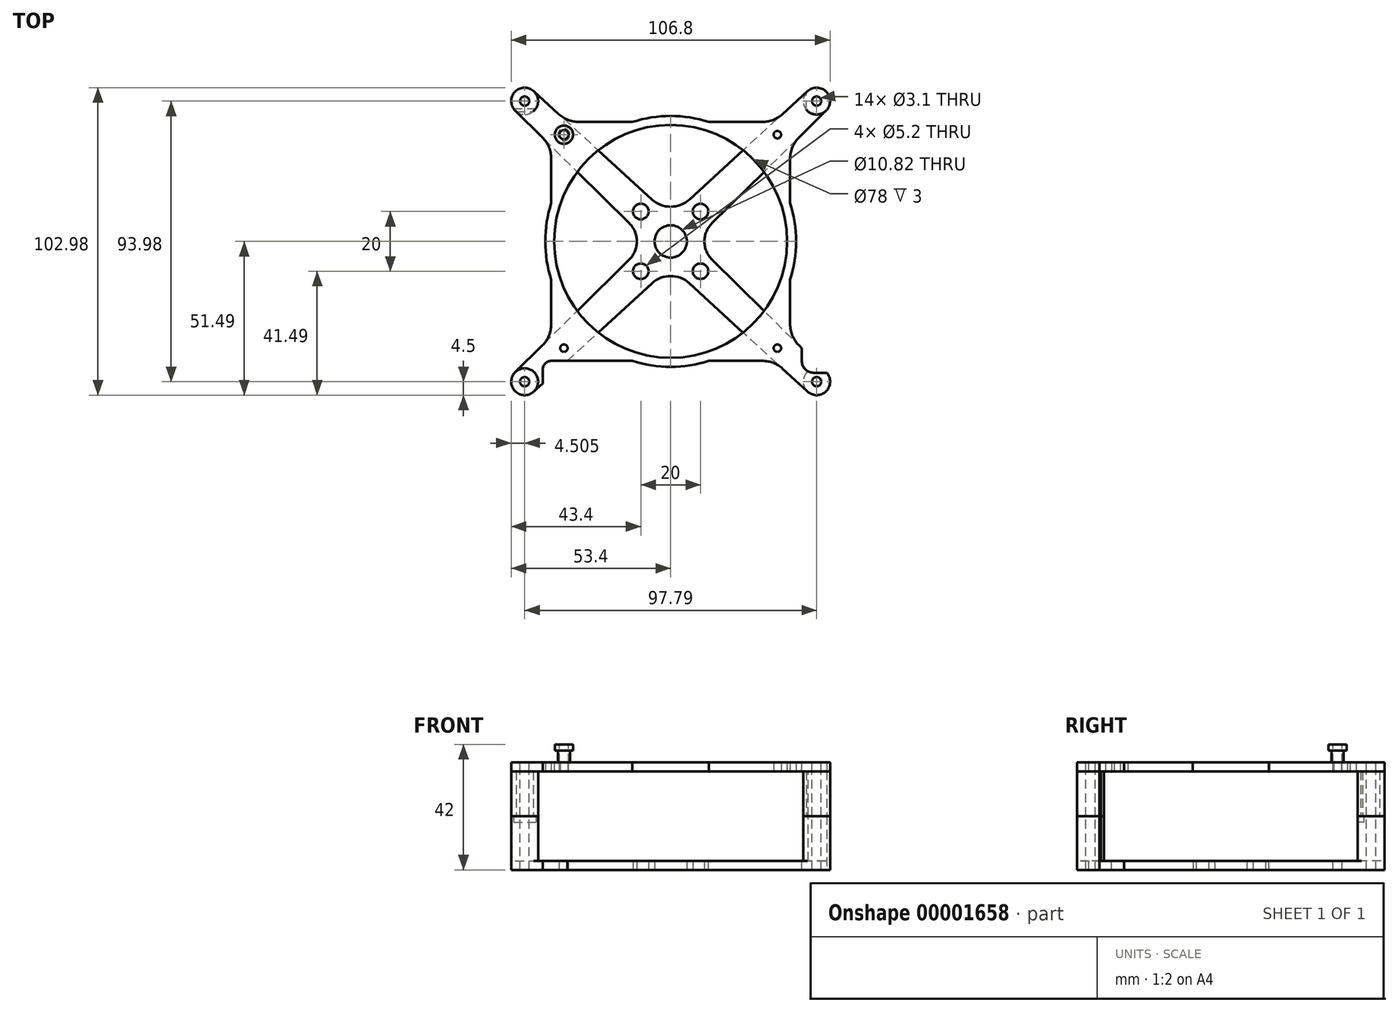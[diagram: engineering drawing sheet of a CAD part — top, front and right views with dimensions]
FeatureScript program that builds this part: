
annotation { "Feature Type Name" : "Feature", "Feature Type Description" : "" }
export const myFeature = defineFeature(function(context is Context, id is Id, definition is map)
    precondition{}
    {
        {
            var Q0;
            Q0=qCreatedBy(makeId("Top.planeOp"),FACE);
            var sketch = newSketch(context, id + "F0", { "sketchPlane" : qUnion([Q0])});
            skLineSegment(sketch, "E0.rect.bottom", {"start": v(48.9, 46.99) * mm, "end": v(-48.9, 46.99) * mm, "construction": true});
            skLineSegment(sketch, "E0.rect.top", {"start": v(48.9, -47) * mm, "end": v(-48.9, -47) * mm, "construction": true});
            skLineSegment(sketch, "E0.rect.left", {"start": v(48.9, 46.99) * mm, "end": v(48.9, -47) * mm, "construction": true});
            skLineSegment(sketch, "E0.rect.right", {"start": v(-48.9, 46.99) * mm, "end": v(-48.9, -47) * mm, "construction": true});
            skPoint(sketch, "E0.rect.middle", {"position": v(0, 0) * mm});
            skLineSegment(sketch, "E1.rect.bottom", {"start": v(10, 10) * mm, "end": v(-10, 10) * mm, "construction": true});
            skLineSegment(sketch, "E1.rect.top", {"start": v(10, -10) * mm, "end": v(-10, -10) * mm, "construction": true});
            skLineSegment(sketch, "E1.rect.left", {"start": v(10, 10) * mm, "end": v(10, -10) * mm, "construction": true});
            skLineSegment(sketch, "E1.rect.right", {"start": v(-10, 10) * mm, "end": v(-10, -10) * mm, "construction": true});
            skCircle(sketch, "E2", {"center": v(-10, 10) * mm, "radius": 2.6 * mm});
            skCircle(sketch, "E3", {"center": v(10, 10) * mm, "radius": 2.6 * mm});
            skCircle(sketch, "E4", {"center": v(10, -10) * mm, "radius": 2.6 * mm});
            skCircle(sketch, "E5", {"center": v(-10, -10) * mm, "radius": 2.6 * mm});
            skArc(sketch, "E6", {"start": v(-45.86, 50.3) * mm, "mid": v(-52.16, 50.1) * mm, "end": v(-52.06, 43.79) * mm});
            skArc(sketch, "E7", {"start": v(52.06, 43.79) * mm, "mid": v(52.16, 50.1) * mm, "end": v(45.86, 50.3) * mm});
            skArc(sketch, "E8", {"start": v(45.86, -50.3) * mm, "mid": v(52.16, -50.1) * mm, "end": v(52.06, -43.79) * mm});
            skArc(sketch, "E9", {"start": v(-52.06, -43.79) * mm, "mid": v(-52.16, -50.1) * mm, "end": v(-45.86, -50.3) * mm});
            skCircle(sketch, "E10", {"center": v(-10, -10) * mm, "radius": 5.5 * mm, "construction": true});
            skCircle(sketch, "E11", {"center": v(10, -10) * mm, "radius": 5.5 * mm, "construction": true});
            skCircle(sketch, "E12", {"center": v(-10, 10) * mm, "radius": 5.5 * mm, "construction": true});
            skCircle(sketch, "E13", {"center": v(10, 10) * mm, "radius": 5.5 * mm, "construction": true});
            skArc(sketch, "E14", {"start": v(-13.86, -6.09) * mm, "mid": v(-11.32, 0) * mm, "end": v(-13.86, 6.09) * mm});
            skLineSegment(sketch, "E15", {"start": v(-52.06, -43.79) * mm, "end": v(-13.86, -6.09) * mm});
            skLineSegment(sketch, "E16", {"start": v(-45.86, -50.3) * mm, "end": v(-6.28, -14.06) * mm});
            skLineSegment(sketch, "E17", {"start": v(45.86, 50.3) * mm, "end": v(6.28, 14.06) * mm});
            skLineSegment(sketch, "E18", {"start": v(52.06, 43.79) * mm, "end": v(13.86, 6.09) * mm});
            skLineSegment(sketch, "E19", {"start": v(-52.06, 43.79) * mm, "end": v(-13.86, 6.09) * mm});
            skLineSegment(sketch, "E20", {"start": v(-45.86, 50.3) * mm, "end": v(-6.28, 14.06) * mm});
            skLineSegment(sketch, "E21", {"start": v(45.86, -50.3) * mm, "end": v(6.28, -14.06) * mm});
            skLineSegment(sketch, "E22", {"start": v(52.06, -43.79) * mm, "end": v(13.86, -6.09) * mm});
            skArc(sketch, "E23", {"start": v(-6.28, 14.06) * mm, "mid": v(0, 11.61) * mm, "end": v(6.28, 14.06) * mm});
            skArc(sketch, "E24", {"start": v(13.86, 6.09) * mm, "mid": v(11.32, 0) * mm, "end": v(13.86, -6.09) * mm});
            skArc(sketch, "E25", {"start": v(6.28, -14.06) * mm, "mid": v(0, -11.61) * mm, "end": v(-6.28, -14.06) * mm});
            skCircle(sketch, "E26", {"center": v(0, 0) * mm, "radius": 5.4 * mm});
            skSolve(sketch);
        }
        {
            var Q0;
            Q0 = qSketchRegion(id + "F0", true);
            extrude(context, id + "F1", {"entities" : qUnion([Q0]), "depth" : 3 * mm});
        }
        {
            var Q0;
            Q0=makeQuery(id+"F1.opExtrude","CAP_FACE",FACE,{"disambiguationData":[OSD([sQuery(id+"F0.wireOp",EDGE,"d0fabe0d-cebb-4a5e-acc7-4882b4730778"),sQuery(id+"F0.wireOp",EDGE,"8b31ac3e-8670-4111-bd45-4e3589581e22"),sQuery(id+"F0.wireOp",EDGE,"b8c4f240-0c61-4009-8258-f043c920e522"),sQuery(id+"F0.wireOp",EDGE,"c1348664-0ed1-4957-8f92-31a3f3ab937f"),sQuery(id+"F0.wireOp",EDGE,"E2"),sQuery(id+"F0.wireOp",EDGE,"E3"),sQuery(id+"F0.wireOp",EDGE,"E4"),sQuery(id+"F0.wireOp",EDGE,"E5"),sQuery(id+"F0.wireOp",EDGE,"E6"),sQuery(id+"F0.wireOp",EDGE,"E7"),sQuery(id+"F0.wireOp",EDGE,"E8"),sQuery(id+"F0.wireOp",EDGE,"E9"),sQuery(id+"F0.wireOp",EDGE,"E14"),sQuery(id+"F0.wireOp",EDGE,"E15"),sQuery(id+"F0.wireOp",EDGE,"E16"),sQuery(id+"F0.wireOp",EDGE,"E17"),sQuery(id+"F0.wireOp",EDGE,"E18"),sQuery(id+"F0.wireOp",EDGE,"E19"),sQuery(id+"F0.wireOp",EDGE,"E20"),sQuery(id+"F0.wireOp",EDGE,"E21"),sQuery(id+"F0.wireOp",EDGE,"E22"),sQuery(id+"F0.wireOp",EDGE,"E23"),sQuery(id+"F0.wireOp",EDGE,"E24"),sQuery(id+"F0.wireOp",EDGE,"E25"),sQuery(id+"F0.wireOp",EDGE,"E26")])],"isStart":false});
            var sketch = newSketch(context, id + "F2", { "sketchPlane" : qUnion([Q0])});
            skCircle(sketch, "E27", {"center": v(-48.9, 46.99) * mm, "radius": 4.5 * mm});
            skCircle(sketch, "E28", {"center": v(48.9, 46.99) * mm, "radius": 4.5 * mm});
            skCircle(sketch, "E29", {"center": v(48.9, -47) * mm, "radius": 4.5 * mm});
            skCircle(sketch, "E30", {"center": v(-48.9, -47) * mm, "radius": 4.5 * mm});
            skSolve(sketch);
        }
        {
            var Q0;
            Q0 = qSketchRegion(id + "F2", true);
            extrude(context, id + "F3", {"entities" : qUnion([Q0]), "operationType" : NewBodyOperationType.ADD, "depth" : 15 * mm});
        }
        {
            var Q0;
            Q0=makeQuery(id+"F3.opExtrude","CAP_FACE",FACE,{"disambiguationData":[OSD([sQuery(id+"F2.wireOp",EDGE,"E27")])],"isStart":false});
            var sketch = newSketch(context, id + "F4", { "sketchPlane" : qUnion([Q0])});
            skCircle(sketch, "E31", {"center": v(-48.9, 46.99) * mm, "radius": 1.25 * mm});
            skCircle(sketch, "E32", {"center": v(48.9, 46.99) * mm, "radius": 1.25 * mm});
            skCircle(sketch, "E33", {"center": v(-48.9, -47) * mm, "radius": 1.25 * mm});
            skCircle(sketch, "E34", {"center": v(48.9, -47) * mm, "radius": 1.25 * mm});
            skSolve(sketch);
        }
        {
            var Q0;
            Q0 = qSketchRegion(id + "F4", true);
            extrude(context, id + "F5", {"entities" : qUnion([Q0]), "operationType" : NewBodyOperationType.REMOVE, "endBound" : BoundingType.THROUGH_ALL, "oppositeDirection" : true, "depth" : 25 * mm});
        }
        {
            var Q0;
            Q0=makeQuery(id+"F3.opExtrude","CAP_FACE",FACE,{"disambiguationData":[OSD([sQuery(id+"F2.wireOp",EDGE,"E27")])],"isStart":false});
            var sketch = newSketch(context, id + "F6", { "sketchPlane" : qUnion([Q0])});
            skArc(sketch, "E35", {"start": v(-46.07, 43.49) * mm, "mid": v(-48.9, 51.49) * mm, "end": v(-51.72, 43.49) * mm});
            skArc(sketch, "E36", {"start": v(45.4, 44.16) * mm, "mid": v(53.4, 47) * mm, "end": v(45.4, 49.82) * mm});
            skArc(sketch, "E37", {"start": v(46.07, -43.5) * mm, "mid": v(48.9, -51.5) * mm, "end": v(51.72, -43.5) * mm});
            skCircle(sketch, "E38", {"center": v(-48.9, -47) * mm, "radius": 4.5 * mm});
            skLineSegment(sketch, "E39", {"start": v(-51.72, 43.49) * mm, "end": v(-46.07, 43.49) * mm});
            skLineSegment(sketch, "E40", {"start": v(45.4, 44.16) * mm, "end": v(45.4, 49.82) * mm});
            skLineSegment(sketch, "E41", {"start": v(46.07, -43.5) * mm, "end": v(51.72, -43.5) * mm});
            skSolve(sketch);
        }
        {
            var Q0;
            Q0 = qSketchRegion(id + "F6", true);
            extrude(context, id + "F7", {"entities" : qUnion([Q0]), "depth" : 15 * mm});
        }
        {
            var Q0;
            Q0=makeQuery(id+"F7.opExtrude","CAP_FACE",FACE,{"disambiguationData":[OSD([sQuery(id+"F6.wireOp",EDGE,"E35")])],"isStart":false});
            var sketch = newSketch(context, id + "F8", { "sketchPlane" : qUnion([Q0])});
            skLineSegment(sketch, "E42.rect.bottom", {"start": v(35.75, 35.75) * mm, "end": v(-35.75, 35.75) * mm, "construction": true});
            skLineSegment(sketch, "E42.rect.top", {"start": v(35.75, -35.75) * mm, "end": v(-35.75, -35.75) * mm, "construction": true});
            skLineSegment(sketch, "E42.rect.left", {"start": v(35.75, 35.75) * mm, "end": v(35.75, -35.75) * mm, "construction": true});
            skLineSegment(sketch, "E42.rect.right", {"start": v(-35.75, 35.75) * mm, "end": v(-35.75, -35.75) * mm, "construction": true});
            skPoint(sketch, "E42.rect.middle", {"position": v(0, 0) * mm});
            skCircle(sketch, "E43", {"center": v(-35.75, 35.75) * mm, "radius": 1.25 * mm});
            skCircle(sketch, "E44", {"center": v(35.75, 35.75) * mm, "radius": 1.25 * mm});
            skCircle(sketch, "E45", {"center": v(35.75, -35.75) * mm, "radius": 1.25 * mm});
            skCircle(sketch, "E46", {"center": v(-35.75, -35.75) * mm, "radius": 1.25 * mm});
            skCircle(sketch, "E47", {"center": v(0, 0) * mm, "radius": 39 * mm});
            skArc(sketch, "E48", {"start": v(-52.06, -43.79) * mm, "mid": v(-52.16, -50.1) * mm, "end": v(-45.86, -50.3) * mm});
            skArc(sketch, "E49", {"start": v(45.86, -50.3) * mm, "mid": v(52.16, -50.1) * mm, "end": v(52.06, -43.79) * mm});
            skArc(sketch, "E50", {"start": v(52.06, 43.79) * mm, "mid": v(52.16, 50.1) * mm, "end": v(45.86, 50.3) * mm});
            skArc(sketch, "E51", {"start": v(-45.86, 50.3) * mm, "mid": v(-52.16, 50.1) * mm, "end": v(-52.06, 43.79) * mm});
            skLineSegment(sketch, "E52", {"start": v(-52.06, 43.79) * mm, "end": v(-42.97, 34.82) * mm});
            skLineSegment(sketch, "E53", {"start": v(-45.86, 50.3) * mm, "end": v(-37.47, 42.63) * mm});
            skLineSegment(sketch, "E54", {"start": v(45.86, 50.3) * mm, "end": v(37.47, 42.63) * mm});
            skLineSegment(sketch, "E55", {"start": v(52.06, 43.79) * mm, "end": v(42.97, 34.82) * mm});
            skLineSegment(sketch, "E56", {"start": v(52.06, -43.79) * mm, "end": v(42.97, -34.82) * mm});
            skLineSegment(sketch, "E57", {"start": v(45.86, -50.3) * mm, "end": v(37.47, -42.63) * mm});
            skLineSegment(sketch, "E58", {"start": v(-45.86, -50.3) * mm, "end": v(-37.47, -42.63) * mm});
            skLineSegment(sketch, "E59", {"start": v(-52.06, -43.79) * mm, "end": v(-42.97, -34.82) * mm});
            skLineSegment(sketch, "E60.rect.bottom", {"start": v(30.72, 40) * mm, "end": v(12.8, 40) * mm});
            skLineSegment(sketch, "E60.rect.top", {"start": v(30.72, -40) * mm, "end": v(12.8, -40) * mm});
            skLineSegment(sketch, "E60.rect.left", {"start": v(40, 27.7) * mm, "end": v(40, 12.8) * mm});
            skLineSegment(sketch, "E60.rect.right", {"start": v(-40, 27.7) * mm, "end": v(-40, 12.8) * mm});
            skPoint(sketch, "E61.orphan", {"position": v(-40, 40) * mm});
            skPoint(sketch, "E62.orphan", {"position": v(-40, -40) * mm});
            skLineSegment(sketch, "E63.trimOffspring", {"start": v(-40, -12.8) * mm, "end": v(-40, -27.7) * mm});
            skPoint(sketch, "E64.orphan", {"position": v(40, -40) * mm});
            skLineSegment(sketch, "E65.trimOffspring", {"start": v(40, -12.8) * mm, "end": v(40, -27.7) * mm});
            skPoint(sketch, "E66.orphan", {"position": v(40, 40) * mm});
            skArc(sketch, "E67.trimOffspring", {"start": v(12.8, 40) * mm, "mid": v(0, 42) * mm, "end": v(-12.8, 40) * mm});
            skLineSegment(sketch, "E68.trimOffspring", {"start": v(-12.8, 40) * mm, "end": v(-30.72, 40) * mm});
            skArc(sketch, "E69.trimOffspring", {"start": v(-40, 12.8) * mm, "mid": v(-42, 0) * mm, "end": v(-40, -12.8) * mm});
            skArc(sketch, "E70.trimOffspring", {"start": v(40, -12.8) * mm, "mid": v(42, 0) * mm, "end": v(40, 12.8) * mm});
            skLineSegment(sketch, "E71.trimOffspring", {"start": v(-12.8, -40) * mm, "end": v(-30.72, -40) * mm});
            skArc(sketch, "E72.trimOffspring", {"start": v(-12.8, -40) * mm, "mid": v(0, -42) * mm, "end": v(12.8, -40) * mm});
            skPoint(sketch, "E73.visualSharp", {"position": v(-40, 31.89) * mm});
            skArc(sketch, "E73.filletArc", {"start": v(-40, 27.7) * mm, "mid": v(-40.77, 31.56) * mm, "end": v(-42.97, 34.82) * mm});
            skPoint(sketch, "E74.visualSharp", {"position": v(-40, -31.89) * mm});
            skArc(sketch, "E74.filletArc", {"start": v(-42.97, -34.82) * mm, "mid": v(-40.77, -31.56) * mm, "end": v(-40, -27.7) * mm});
            skPoint(sketch, "E75.visualSharp", {"position": v(-34.6, -40) * mm});
            skArc(sketch, "E75.filletArc", {"start": v(-30.72, -40) * mm, "mid": v(-34.34, -40.68) * mm, "end": v(-37.47, -42.63) * mm});
            skPoint(sketch, "E76.visualSharp", {"position": v(34.6, -40) * mm});
            skArc(sketch, "E76.filletArc", {"start": v(37.47, -42.63) * mm, "mid": v(34.34, -40.68) * mm, "end": v(30.72, -40) * mm});
            skPoint(sketch, "E77.visualSharp", {"position": v(40, -31.89) * mm});
            skArc(sketch, "E77.filletArc", {"start": v(40, -27.7) * mm, "mid": v(40.77, -31.56) * mm, "end": v(42.97, -34.82) * mm});
            skPoint(sketch, "E78.visualSharp", {"position": v(40, 31.89) * mm});
            skArc(sketch, "E78.filletArc", {"start": v(42.97, 34.82) * mm, "mid": v(40.77, 31.56) * mm, "end": v(40, 27.7) * mm});
            skPoint(sketch, "E79.visualSharp", {"position": v(34.6, 40) * mm});
            skArc(sketch, "E79.filletArc", {"start": v(30.72, 40) * mm, "mid": v(34.34, 40.68) * mm, "end": v(37.47, 42.63) * mm});
            skPoint(sketch, "E80.visualSharp", {"position": v(-34.6, 40) * mm});
            skArc(sketch, "E80.filletArc", {"start": v(-37.47, 42.63) * mm, "mid": v(-34.34, 40.68) * mm, "end": v(-30.72, 40) * mm});
            skSolve(sketch);
        }
        {
            var Q0;
            Q0 = qSketchRegion(id + "F8", true);
            extrude(context, id + "F9", {"entities" : qUnion([Q0]), "depth" : 3 * mm});
        }
        {
            var Q0;
            Q0=makeQuery(id+"F9.opExtrude","CAP_FACE",FACE,{"disambiguationData":[OSD([sQuery(id+"F8.wireOp",EDGE,"E43"),sQuery(id+"F8.wireOp",EDGE,"E44"),sQuery(id+"F8.wireOp",EDGE,"E45"),sQuery(id+"F8.wireOp",EDGE,"E46"),sQuery(id+"F8.wireOp",EDGE,"E47"),sQuery(id+"F8.wireOp",EDGE,"687bd6d6-6aec-43aa-978a-a651606573d6"),sQuery(id+"F8.wireOp",EDGE,"E48"),sQuery(id+"F8.wireOp",EDGE,"E49"),sQuery(id+"F8.wireOp",EDGE,"E50"),sQuery(id+"F8.wireOp",EDGE,"E51"),sQuery(id+"F8.wireOp",EDGE,"E52"),sQuery(id+"F8.wireOp",EDGE,"E53"),sQuery(id+"F8.wireOp",EDGE,"E54"),sQuery(id+"F8.wireOp",EDGE,"E55"),sQuery(id+"F8.wireOp",EDGE,"E56"),sQuery(id+"F8.wireOp",EDGE,"E57"),sQuery(id+"F8.wireOp",EDGE,"E58"),sQuery(id+"F8.wireOp",EDGE,"E59"),sQuery(id+"F8.wireOp",EDGE,"161f5221-b585-4942-8812-eb4c8e719fd1.trimOffspring"),sQuery(id+"F8.wireOp",EDGE,"33abffde-fc44-4a8e-acad-815204f06dd8.trimOffspring"),sQuery(id+"F8.wireOp",EDGE,"e672300c-3f6b-4d4b-81d5-837dd4541bc1.trimOffspring")])],"isStart":false});
            var sketch = newSketch(context, id + "F10", { "sketchPlane" : qUnion([Q0])});
            skCircle(sketch, "E81", {"center": v(-48.9, 46.99) * mm, "radius": 1.55 * mm});
            skCircle(sketch, "E82", {"center": v(48.9, 46.99) * mm, "radius": 1.55 * mm});
            skCircle(sketch, "E83", {"center": v(48.9, -47) * mm, "radius": 1.55 * mm});
            skCircle(sketch, "E84", {"center": v(-48.9, -47) * mm, "radius": 1.55 * mm});
            skSolve(sketch);
        }
        {
            var Q0;
            Q0 = qSketchRegion(id + "F10", true);
            extrude(context, id + "F11", {"entities" : qUnion([Q0]), "operationType" : NewBodyOperationType.REMOVE, "endBound" : BoundingType.THROUGH_ALL, "oppositeDirection" : true, "depth" : 25 * mm});
        }
        {
            var Q0;
            Q0=makeQuery(id+"F9.opExtrude","CAP_FACE",FACE,{"disambiguationData":[OSD([sQuery(id+"F8.wireOp",EDGE,"E43"),sQuery(id+"F8.wireOp",EDGE,"E44"),sQuery(id+"F8.wireOp",EDGE,"E45"),sQuery(id+"F8.wireOp",EDGE,"E46"),sQuery(id+"F8.wireOp",EDGE,"E47"),sQuery(id+"F8.wireOp",EDGE,"687bd6d6-6aec-43aa-978a-a651606573d6"),sQuery(id+"F8.wireOp",EDGE,"E48"),sQuery(id+"F8.wireOp",EDGE,"E49"),sQuery(id+"F8.wireOp",EDGE,"E50"),sQuery(id+"F8.wireOp",EDGE,"E51"),sQuery(id+"F8.wireOp",EDGE,"E52"),sQuery(id+"F8.wireOp",EDGE,"E53"),sQuery(id+"F8.wireOp",EDGE,"E54"),sQuery(id+"F8.wireOp",EDGE,"E55"),sQuery(id+"F8.wireOp",EDGE,"E56"),sQuery(id+"F8.wireOp",EDGE,"E57"),sQuery(id+"F8.wireOp",EDGE,"E58"),sQuery(id+"F8.wireOp",EDGE,"E59"),sQuery(id+"F8.wireOp",EDGE,"161f5221-b585-4942-8812-eb4c8e719fd1.trimOffspring"),sQuery(id+"F8.wireOp",EDGE,"33abffde-fc44-4a8e-acad-815204f06dd8.trimOffspring"),sQuery(id+"F8.wireOp",EDGE,"e672300c-3f6b-4d4b-81d5-837dd4541bc1.trimOffspring")])],"isStart":false});
            var sketch = newSketch(context, id + "F12", { "sketchPlane" : qUnion([Q0])});
            skCircle(sketch, "E85", {"center": v(-35.75, 35.75) * mm, "radius": 2.05 * mm});
            skSolve(sketch);
        }
        {
            var Q0;
            Q0 = qSketchRegion(id + "F12", true);
            extrude(context, id + "F13", {"entities" : qUnion([Q0]), "depth" : 4 * mm});
        }
        {
            var Q0;
            Q0=makeQuery(id+"F13.opExtrude","CAP_FACE",FACE,{"disambiguationData":[OSD([sQuery(id+"F12.wireOp",EDGE,"E85")])],"isStart":false});
            var sketch = newSketch(context, id + "F14", { "sketchPlane" : qUnion([Q0])});
            skCircle(sketch, "E86", {"center": v(-35.75, 35.75) * mm, "radius": 3.05 * mm});
            skSolve(sketch);
        }
        {
            var Q0;
            Q0 = qSketchRegion(id + "F14", true);
            extrude(context, id + "F15", {"entities" : qUnion([Q0]), "operationType" : NewBodyOperationType.ADD, "depth" : 2 * mm});
        }
        {
            var Q0;
            Q0=makeQuery(id+"F15.opExtrude","CAP_FACE",FACE,{"disambiguationData":[OSD([sQuery(id+"F14.wireOp",EDGE,"E86")])],"isStart":false});
            var sketch = newSketch(context, id + "F16", { "sketchPlane" : qUnion([Q0])});
            skCircle(sketch, "E87", {"center": v(-35.75, 35.75) * mm, "radius": 1.55 * mm});
            skSolve(sketch);
        }
        {
            var Q0;
            Q0 = qSketchRegion(id + "F16", true);
            extrude(context, id + "F17", {"entities" : qUnion([Q0]), "operationType" : NewBodyOperationType.REMOVE, "endBound" : BoundingType.THROUGH_ALL, "oppositeDirection" : true, "depth" : 25 * mm});
        }
        {
            var Q0;
            Q0=makeQuery(id+"F3.opExtrude","CAP_FACE",FACE,{"disambiguationData":[OSD([sQuery(id+"F2.wireOp",EDGE,"E27")])],"isStart":false});
            var sketch = newSketch(context, id + "F18", { "sketchPlane" : qUnion([Q0])});
            skLineSegment(sketch, "E88.bottom", {"start": v(-53.4, 44.49) * mm, "end": v(-44.4, 44.49) * mm});
            skLineSegment(sketch, "E88.top", {"start": v(-53.4, 41.49) * mm, "end": v(-44.4, 41.49) * mm});
            skLineSegment(sketch, "E88.left", {"start": v(-53.4, 44.49) * mm, "end": v(-53.4, 41.49) * mm});
            skLineSegment(sketch, "E88.right", {"start": v(-44.4, 44.49) * mm, "end": v(-44.4, 41.49) * mm});
            skPoint(sketch, "E89", {"position": v(-48.9, 46.99) * mm});
            skSolve(sketch);
        }
        {
            var Q0;
            Q0 = qSketchRegion(id + "F18", true);
            extrude(context, id + "F19", {"entities" : qUnion([Q0]), "operationType" : NewBodyOperationType.REMOVE, "oppositeDirection" : true, "depth" : 2 * mm});
        }
        {
            var Q0;
            Q0=makeQuery(id+"F9.opExtrude","CAP_FACE",FACE,{"disambiguationData":[OSD([sQuery(id+"F8.wireOp",EDGE,"E43"),sQuery(id+"F8.wireOp",EDGE,"E44"),sQuery(id+"F8.wireOp",EDGE,"E45"),sQuery(id+"F8.wireOp",EDGE,"E46"),sQuery(id+"F8.wireOp",EDGE,"E47"),sQuery(id+"F8.wireOp",EDGE,"687bd6d6-6aec-43aa-978a-a651606573d6"),sQuery(id+"F8.wireOp",EDGE,"E48"),sQuery(id+"F8.wireOp",EDGE,"E49"),sQuery(id+"F8.wireOp",EDGE,"E50"),sQuery(id+"F8.wireOp",EDGE,"E51"),sQuery(id+"F8.wireOp",EDGE,"E52"),sQuery(id+"F8.wireOp",EDGE,"E53"),sQuery(id+"F8.wireOp",EDGE,"E54"),sQuery(id+"F8.wireOp",EDGE,"E55"),sQuery(id+"F8.wireOp",EDGE,"E56"),sQuery(id+"F8.wireOp",EDGE,"E57"),sQuery(id+"F8.wireOp",EDGE,"E58"),sQuery(id+"F8.wireOp",EDGE,"E59"),sQuery(id+"F8.wireOp",EDGE,"161f5221-b585-4942-8812-eb4c8e719fd1.trimOffspring"),sQuery(id+"F8.wireOp",EDGE,"33abffde-fc44-4a8e-acad-815204f06dd8.trimOffspring"),sQuery(id+"F8.wireOp",EDGE,"e672300c-3f6b-4d4b-81d5-837dd4541bc1.trimOffspring")])],"isStart":false});
            var sketch = newSketch(context, id + "F20", { "sketchPlane" : qUnion([Q0])});
            skLineSegment(sketch, "E90.bottom", {"start": v(47.9, -44) * mm, "end": v(52.9, -44) * mm});
            skLineSegment(sketch, "E90.top", {"start": v(43.9, -35) * mm, "end": v(52.9, -35) * mm});
            skLineSegment(sketch, "E90.left", {"start": v(43.9, -40) * mm, "end": v(43.9, -35) * mm});
            skLineSegment(sketch, "E90.right", {"start": v(52.9, -44) * mm, "end": v(52.9, -35) * mm});
            skPoint(sketch, "E91", {"position": v(48.9, -47) * mm});
            skPoint(sketch, "E92.visualSharp", {"position": v(43.9, -44) * mm});
            skArc(sketch, "E92.filletArc", {"start": v(43.9, -40) * mm, "mid": v(45.07, -42.82) * mm, "end": v(47.9, -44) * mm});
            skLineSegment(sketch, "E93.bottom", {"start": v(-42.9, -52.18) * mm, "end": v(-30.72, -52.18) * mm});
            skLineSegment(sketch, "E93.top", {"start": v(-39.9, -40) * mm, "end": v(-30.72, -40) * mm});
            skLineSegment(sketch, "E93.left", {"start": v(-42.9, -43) * mm, "end": v(-42.9, -52.18) * mm});
            skLineSegment(sketch, "E93.right", {"start": v(-30.72, -40) * mm, "end": v(-30.72, -52.18) * mm});
            skPoint(sketch, "E94", {"position": v(-48.9, -47) * mm});
            skPoint(sketch, "E95.visualSharp", {"position": v(-42.9, -40) * mm});
            skArc(sketch, "E95.filletArc", {"start": v(-39.9, -40) * mm, "mid": v(-42.02, -40.88) * mm, "end": v(-42.9, -43) * mm});
            skSolve(sketch);
        }
        {
            var Q0;
            Q0 = qSketchRegion(id + "F20", true);
            extrude(context, id + "F21", {"entities" : qUnion([Q0]), "operationType" : NewBodyOperationType.REMOVE, "endBound" : BoundingType.THROUGH_ALL, "oppositeDirection" : true, "depth" : 25 * mm});
        }
    });
